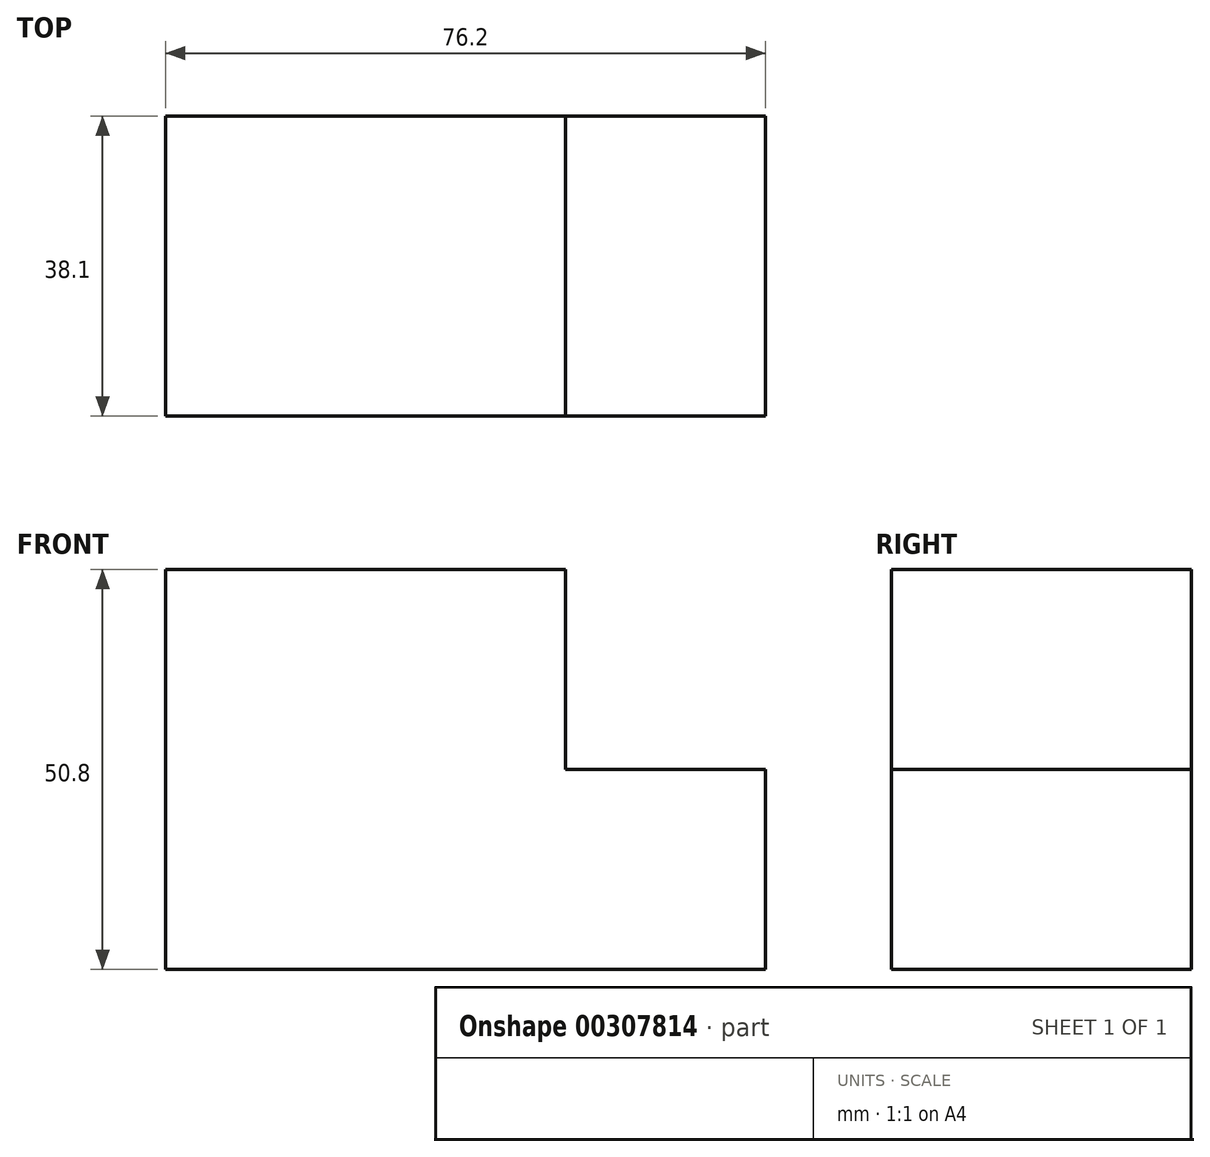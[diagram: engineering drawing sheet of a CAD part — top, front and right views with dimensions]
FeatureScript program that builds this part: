
annotation { "Feature Type Name" : "Feature", "Feature Type Description" : "" }
export const myFeature = defineFeature(function(context is Context, id is Id, definition is map)
    precondition{}
    {
        {
            var Q0;
            Q0=qCreatedBy(makeId("Front.planeOp"),FACE);
            var sketch = newSketch(context, id + "F0", { "sketchPlane" : qUnion([Q0])});
            skLineSegment(sketch, "E0", {"start": v(-35.22, -43.87) * mm, "end": v(40.98, -43.87) * mm});
            skLineSegment(sketch, "E1", {"start": v(40.98, -43.87) * mm, "end": v(40.98, -18.47) * mm});
            skLineSegment(sketch, "E2", {"start": v(40.98, -18.47) * mm, "end": v(15.58, -18.47) * mm});
            skLineSegment(sketch, "E3", {"start": v(15.58, -18.47) * mm, "end": v(15.58, 6.93) * mm});
            skLineSegment(sketch, "E4", {"start": v(15.58, 6.93) * mm, "end": v(-35.22, 6.93) * mm});
            skLineSegment(sketch, "E5", {"start": v(-35.22, 6.93) * mm, "end": v(-35.22, -43.87) * mm});
            skSolve(sketch);
        }
        {
            var Q0;
            Q0=makeQuery(id+"F0.imprint","IMPRINT",FACE,{"disambiguationData":[TD([[makeQuery(id+"F0.imprint","IMPRINT",EDGE,{"derivedFrom":sQuery(id+"F0.wireOp",EDGE,"E0")}),1.0]])]});
            extrude(context, id + "F1", {"entities" : qUnion([Q0]), "depth" : 38.1 * mm});
        }
    });
